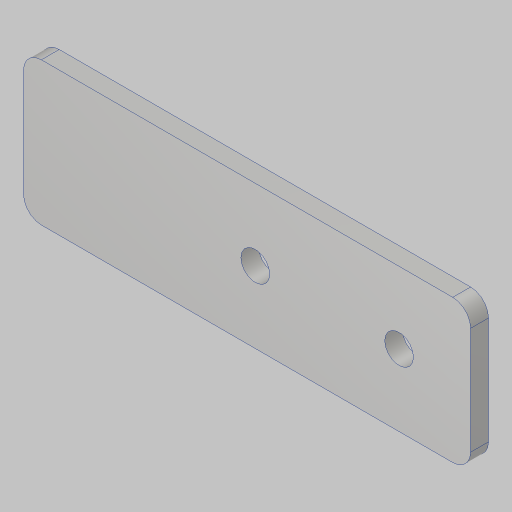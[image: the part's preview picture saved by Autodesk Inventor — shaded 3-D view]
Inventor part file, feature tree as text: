
AUTODESK INVENTOR PART (.ipt)
format: ipt  version: 2023.5 (Build 275446000, 446)  size: 116,224 bytes
history: native  units: in
note: dims shown in document units (in); Inventor stores cm internally (conversion verified against a paired STEP export)
features: sketch x2, extrude x1, hole x1, fillet x1
ambient origin geometry x8: Origin, YZ Plane, XZ Plane, XY Plane, X Axis, Y Axis, Z Axis, Center Point
bodies: Solid1 (feature_tree)
feature tree (5):
  extrude  "Extrusion1"  Depth=3.125in
  hole  "Hole2"  [1 undecoded]
  fillet  "Fillet2"  Radius=2.625in
  sketch  "Sketch1"  dims[d2=0.125in d3=0.0in d15=3.125in]
  sketch  "Sketch3"  dims[d16=1.0in d17=1.005in d18=2.625in d19=0.201in d20=0.75in d21=0.385in d22=0.25in d23=0.5635in d24=1.0in d25=0.8108in d26=0.125in]
note: 1 required parameter value undecoded (feature->parameter linkage not recoverable at this tier; creation-order binding heuristic only, values carry confidence <= 0.55)
